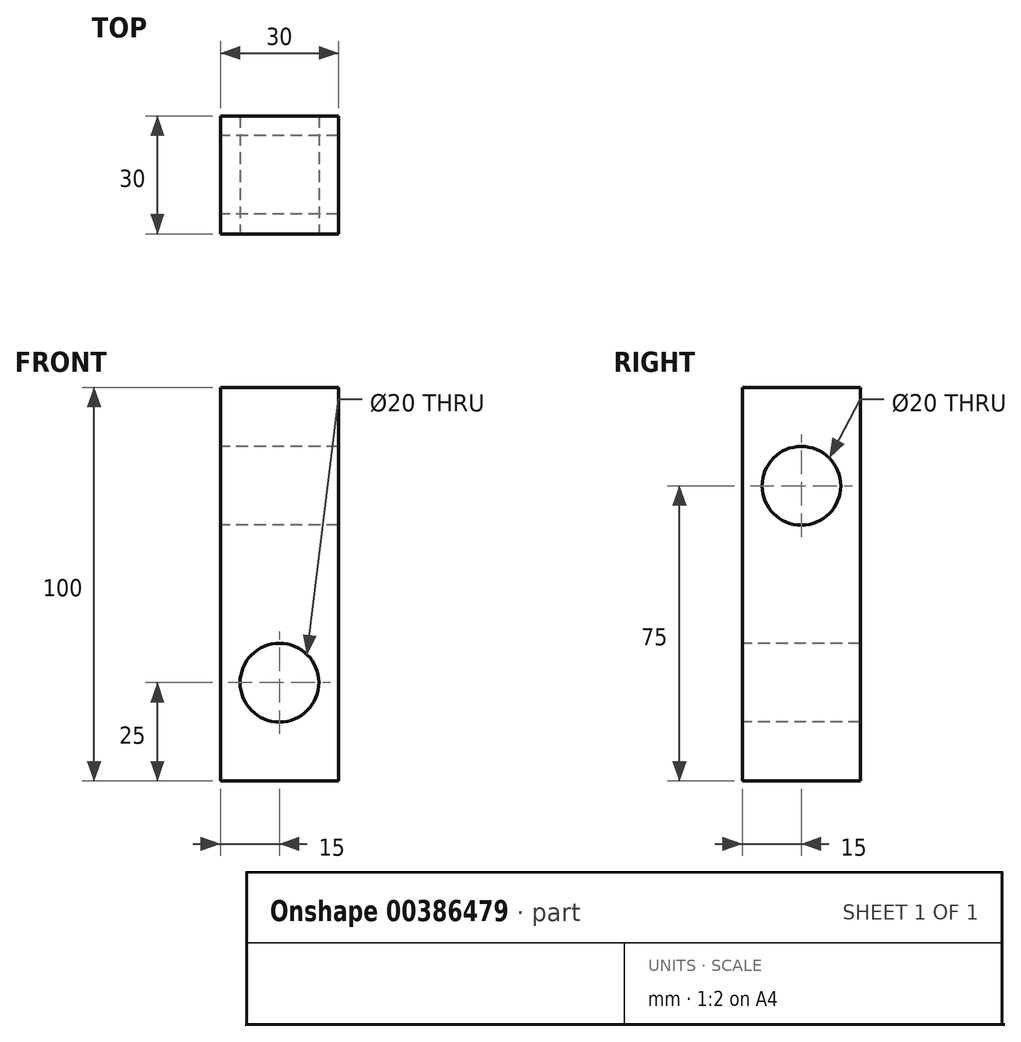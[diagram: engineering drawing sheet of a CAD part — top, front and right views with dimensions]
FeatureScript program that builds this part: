
annotation { "Feature Type Name" : "Feature", "Feature Type Description" : "" }
export const myFeature = defineFeature(function(context is Context, id is Id, definition is map)
    precondition{}
    {
        {
            var Q0;
            Q0=qCreatedBy(makeId("Front.planeOp"),FACE);
            var sketch = newSketch(context, id + "F0", { "sketchPlane" : qUnion([Q0])});
            skLineSegment(sketch, "E0.bottom", {"start": v(0, 0) * mm, "end": v(30, 0) * mm});
            skLineSegment(sketch, "E0.top", {"start": v(0, 100) * mm, "end": v(30, 100) * mm});
            skLineSegment(sketch, "E0.left", {"start": v(0, 0) * mm, "end": v(0, 100) * mm});
            skLineSegment(sketch, "E0.right", {"start": v(30, 0) * mm, "end": v(30, 100) * mm});
            skCircle(sketch, "E1", {"center": v(15, 25) * mm, "radius": 10 * mm});
            skPoint(sketch, "E1.centerSnap0", {"position": v(15, 0) * mm});
            skSolve(sketch);
        }
        {
            var Q0;
            Q0=qCreatedBy(makeId("Right.planeOp"),FACE);
            var sketch = newSketch(context, id + "F1", { "sketchPlane" : qUnion([Q0])});
            skLineSegment(sketch, "E2.bottom", {"start": v(0, 0) * mm, "end": v(30, 0) * mm});
            skLineSegment(sketch, "E2.top", {"start": v(0, 100) * mm, "end": v(30, 100) * mm});
            skLineSegment(sketch, "E2.left", {"start": v(0, 0) * mm, "end": v(0, 100) * mm});
            skLineSegment(sketch, "E2.right", {"start": v(30, 0) * mm, "end": v(30, 100) * mm});
            skCircle(sketch, "E3", {"center": v(15, 75) * mm, "radius": 10 * mm});
            skPoint(sketch, "E3.centerSnap0", {"position": v(15, 0) * mm});
            skSolve(sketch);
        }
        {
            var Q0;
            Q0=makeQuery(id+"F0.imprint","IMPRINT",FACE,{"disambiguationData":[TD([[makeQuery(id+"F0.imprint","IMPRINT",EDGE,{"derivedFrom":sQuery(id+"F0.wireOp",EDGE,"E0.bottom")}),1.0]])]});
            extrude(context, id + "F2", {"entities" : qUnion([Q0]), "depth" : -30 * mm});
        }
        {
            var Q0;
            Q0=sQuery(id+"F1.wireOp",VERTEX,"E3.center");
            var Q1;
            Q1=makeQuery(id+"F2.opExtrude","SWEPT_BODY",BODY,{"disambiguationData":[OSD([sQuery(id+"F0.wireOp",EDGE,"E0.bottom"),sQuery(id+"F0.wireOp",EDGE,"E0.top"),sQuery(id+"F0.wireOp",EDGE,"E0.left"),sQuery(id+"F0.wireOp",EDGE,"E0.right"),sQuery(id+"F0.wireOp",EDGE,"E1")])]});
            hole(context, id + "F3", {"style" : HoleStyle.SIMPLE, "endStyle" : HoleEndStyle.THROUGH, "oppositeDirection" : true, "holeDiameter" : 20 * mm, "isTappedThrough" : true, "tappedDepth" : 12.7 * mm, "tapClearance" : 3, "locations" : qUnion([Q0]), "scope" : qUnion([Q1])});
        }
    });
